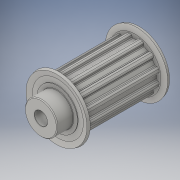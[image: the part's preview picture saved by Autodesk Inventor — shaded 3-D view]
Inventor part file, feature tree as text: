
AUTODESK INVENTOR PART (.ipt)
format: ipt  version: 2016 (Build 200138000, 138)  size: 307,712 bytes
history: native  units: in
note: dims shown in document units (in); Inventor stores cm internally (conversion verified against a paired STEP export)
features: other x3, hole x1, chamfer x1, sketch x1
ambient origin geometry x8: Origin, YZ Plane, XZ Plane, XY Plane, X Axis, Y Axis, Z Axis, Center Point
bodies: Solid1 (feature_tree)
feature tree (6):
  other  "Brecoflex T5 12 tooth.ipt"
  hole  "Hole1"  [1 undecoded]
  chamfer  "Chamfer1"  [1 undecoded]
  other  "Solid1::Brecoflex T5 12 tooth.ipt"
  other  "TaggingFeature1"
  sketch  "Sketch1"  dims[d0=0.3937in d1=0.187in d2=0.75in d3=0.375in d4=0.25in d5=0.5635in d6=1.0in d7=0.8108in d8=0.0039in d9=0.125in d10=45.0deg]
note: 2 required parameter values undecoded (feature->parameter linkage not recoverable at this tier; creation-order binding heuristic only, values carry confidence <= 0.55)
